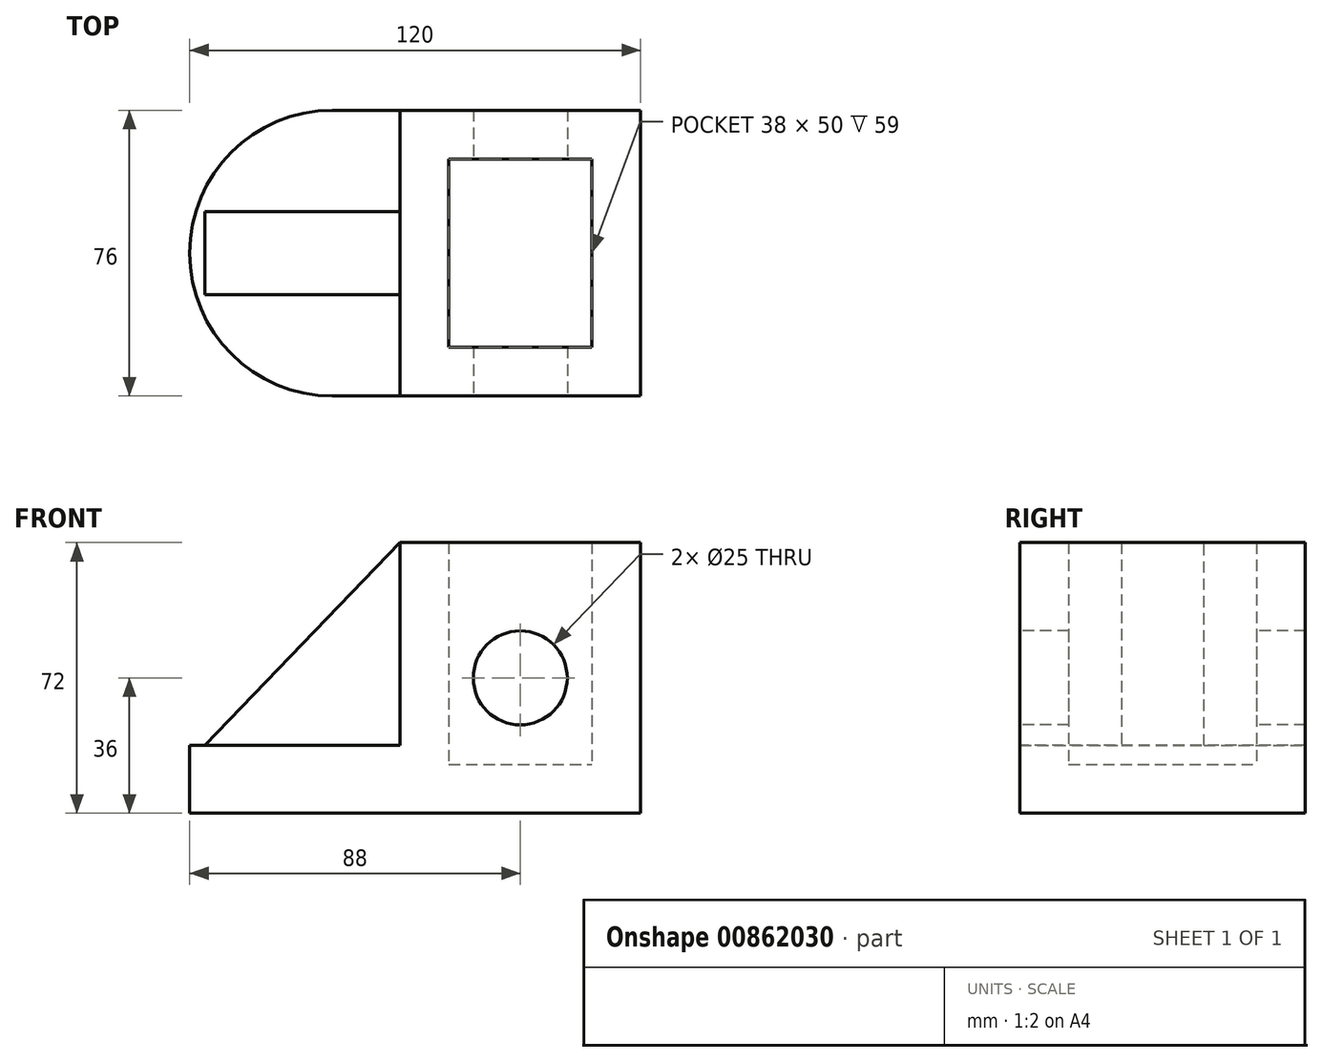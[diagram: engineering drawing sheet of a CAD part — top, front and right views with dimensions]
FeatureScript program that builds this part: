
annotation { "Feature Type Name" : "Feature", "Feature Type Description" : "" }
export const myFeature = defineFeature(function(context is Context, id is Id, definition is map)
    precondition{}
    {
        {
            var Q0;
            Q0=qCreatedBy(makeId("Top.planeOp"),FACE);
            var sketch = newSketch(context, id + "F0", { "sketchPlane" : qUnion([Q0])});
            skLineSegment(sketch, "E0.bottom", {"start": v(0, 0) * mm, "end": v(64, 0) * mm});
            skLineSegment(sketch, "E0.top", {"start": v(0, 76) * mm, "end": v(64, 76) * mm});
            skLineSegment(sketch, "E0.left", {"start": v(0, 0) * mm, "end": v(0, 76) * mm});
            skLineSegment(sketch, "E0.right", {"start": v(64, 0) * mm, "end": v(64, 76) * mm});
            skSolve(sketch);
        }
        {
            var Q0;
            Q0 = qSketchRegion(id + "F0", true);
            extrude(context, id + "F1", {"entities" : qUnion([Q0]), "depth" : 72 * mm, "offsetDistance" : 25 * mm});
        }
        {
            var Q0;
            Q0=makeQuery(id+"F1.opExtrude","CAP_FACE",FACE,{"disambiguationData":[OSD([sQuery(id+"F0.wireOp",EDGE,"E0.bottom"),sQuery(id+"F0.wireOp",EDGE,"E0.top"),sQuery(id+"F0.wireOp",EDGE,"E0.left"),sQuery(id+"F0.wireOp",EDGE,"E0.right")])],"isStart":false});
            shell(context, id + "F2", {"entities" : qUnion([Q0]), "thickness" : 13 * mm});
        }
        {
            var Q0;
            Q0=makeQuery(id+"F1.opExtrude","SWEPT_FACE",FACE,{"disambiguationData":[OSD([sQuery(id+"F0.wireOp",EDGE,"E0.bottom")])]});
            var sketch = newSketch(context, id + "F3", { "sketchPlane" : qUnion([Q0])});
            skCircle(sketch, "E1", {"center": v(32, 36) * mm, "radius": 12.5 * mm});
            skSolve(sketch);
        }
        {
            var Q0;
            Q0=makeQuery(id+"F3.imprint","IMPRINT",FACE,{"disambiguationData":[TD([[makeQuery(id+"F3.imprint","IMPRINT",EDGE,{"derivedFrom":sQuery(id+"F3.wireOp",EDGE,"E1")}),1.0]])]});
            extrude(context, id + "F4", {"entities" : qUnion([Q0]), "operationType" : NewBodyOperationType.REMOVE, "oppositeDirection" : true, "depth" : 100 * mm, "offsetDistance" : 25 * mm});
        }
        {
            var Q0;
            Q0=makeQuery(id+"F1.opExtrude","SWEPT_FACE",FACE,{"disambiguationData":[OSD([sQuery(id+"F0.wireOp",EDGE,"E0.left")])]});
            var sketch = newSketch(context, id + "F5", { "sketchPlane" : qUnion([Q0])});
            skLineSegment(sketch, "E2", {"start": v(0, 0) * mm, "end": v(0, 18) * mm});
            skLineSegment(sketch, "E3", {"start": v(0, 18) * mm, "end": v(-76, 18) * mm});
            skLineSegment(sketch, "E4", {"start": v(-76, 18) * mm, "end": v(-76, 0) * mm});
            skLineSegment(sketch, "E5", {"start": v(-76, 0) * mm, "end": v(0, 0) * mm});
            skSolve(sketch);
        }
        {
            var Q0;
            Q0=makeQuery(id+"F5.imprint","IMPRINT",FACE,{"disambiguationData":[TD([[makeQuery(id+"F5.imprint","IMPRINT",EDGE,{"derivedFrom":sQuery(id+"F5.wireOp",EDGE,"E2")}),-1.0]])]});
            extrude(context, id + "F6", {"entities" : qUnion([Q0]), "operationType" : NewBodyOperationType.ADD, "depth" : 56 * mm, "offsetDistance" : 25 * mm});
        }
        {
            var Q0;
            Q0=makeQuery(id+"F6.opExtrude","SWEPT_FACE",FACE,{"disambiguationData":[OSD([sQuery(id+"F5.wireOp",EDGE,"E3")])]});
            var sketch = newSketch(context, id + "F7", { "sketchPlane" : qUnion([Q0])});
            skLineSegment(sketch, "E6", {"start": v(0, 76) * mm, "end": v(-18, 76) * mm});
            skLineSegment(sketch, "E7", {"start": v(-18, 0) * mm, "end": v(0, 0) * mm});
            skArc(sketch, "E8", {"start": v(-18, 76) * mm, "mid": v(-56, 38) * mm, "end": v(-18, 0) * mm});
            skSolve(sketch);
        }
        {
            var Q0;
            {var subQ0=sQuery(id+"F7.wireOp",EDGE,"E8");var subQ1=sQuery(id+"F5.wireOp",EDGE,"E3");var subQ4=makeQuery(id+"F6.opExtrude","CAP_EDGE",EDGE,{"disambiguationData":[OSD([subQ1])],"isStart":false});var subQ5=makeQuery(id+"F7.imprint","INTERSECT",VERTEX,{"derivedFrom":[subQ4,subQ0]});Q0=makeQuery(id+"F7.imprint","IMPRINT",FACE,{"disambiguationData":[TD([[makeQuery(id+"F7.imprint","IMPRINT",EDGE,{"disambiguationData":[TD([[subQ5,-1.0]])],"derivedFrom":subQ4}),-1.0]])]});}
            var Q1;
            {var subQ0=sQuery(id+"F7.wireOp",EDGE,"E8");var subQ1=sQuery(id+"F5.wireOp",EDGE,"E3");var subQ4=makeQuery(id+"F6.opExtrude","CAP_EDGE",EDGE,{"disambiguationData":[OSD([subQ1])],"isStart":false});var subQ5=makeQuery(id+"F7.imprint","INTERSECT",VERTEX,{"derivedFrom":[subQ4,subQ0]});Q1=makeQuery(id+"F7.imprint","IMPRINT",FACE,{"disambiguationData":[TD([[makeQuery(id+"F7.imprint","IMPRINT",EDGE,{"disambiguationData":[TD([[subQ5,1.0]])],"derivedFrom":subQ4}),-1.0]])]});}
            extrude(context, id + "F8", {"entities" : qUnion([Q0, Q1]), "operationType" : NewBodyOperationType.REMOVE, "oppositeDirection" : true, "depth" : 25 * mm, "offsetDistance" : 25 * mm});
        }
        {
            var Q0;
            Q0=makeQuery(id+"F1.opExtrude","SWEPT_FACE",FACE,{"disambiguationData":[OSD([sQuery(id+"F0.wireOp",EDGE,"E0.left")])]});
            var sketch = newSketch(context, id + "F9", { "sketchPlane" : qUnion([Q0])});
            skLineSegment(sketch, "E9", {"start": v(-27, 72) * mm, "end": v(-27, 18) * mm});
            skLineSegment(sketch, "E10", {"start": v(-27, 18) * mm, "end": v(-49, 18) * mm});
            skLineSegment(sketch, "E11", {"start": v(-49, 18) * mm, "end": v(-49, 72) * mm});
            skLineSegment(sketch, "E12", {"start": v(-49, 72) * mm, "end": v(-27, 72) * mm});
            skSolve(sketch);
        }
        {
            var Q0;
            Q0 = qSketchRegion(id + "F9", true);
            extrude(context, id + "F10", {"entities" : qUnion([Q0]), "operationType" : NewBodyOperationType.ADD, "depth" : 52 * mm, "offsetDistance" : 25 * mm});
        }
        {
            var Q0;
            Q0=makeQuery(id+"F10.opExtrude","SWEPT_FACE",FACE,{"disambiguationData":[OSD([sQuery(id+"F9.wireOp",EDGE,"E9")])]});
            var sketch = newSketch(context, id + "F11", { "sketchPlane" : qUnion([Q0])});
            skLineSegment(sketch, "E13", {"start": v(0, 72) * mm, "end": v(-52, 18) * mm});
            skSolve(sketch);
        }
        {
            var Q0;
            Q0 = qSketchRegion(id + "F11", true);
            var Q1;
            Q1=makeQuery(id+"F11.imprint","IMPRINT",FACE,{"disambiguationData":[TD([[makeQuery(id+"F11.imprint","IMPRINT",EDGE,{"derivedFrom":sQuery(id+"F11.wireOp",EDGE,"E13")}),-1.0]])]});
            extrude(context, id + "F12", {"entities" : qUnion([Q0, Q1]), "operationType" : NewBodyOperationType.REMOVE, "oppositeDirection" : true, "depth" : 25 * mm, "offsetDistance" : 25 * mm});
        }
    });
